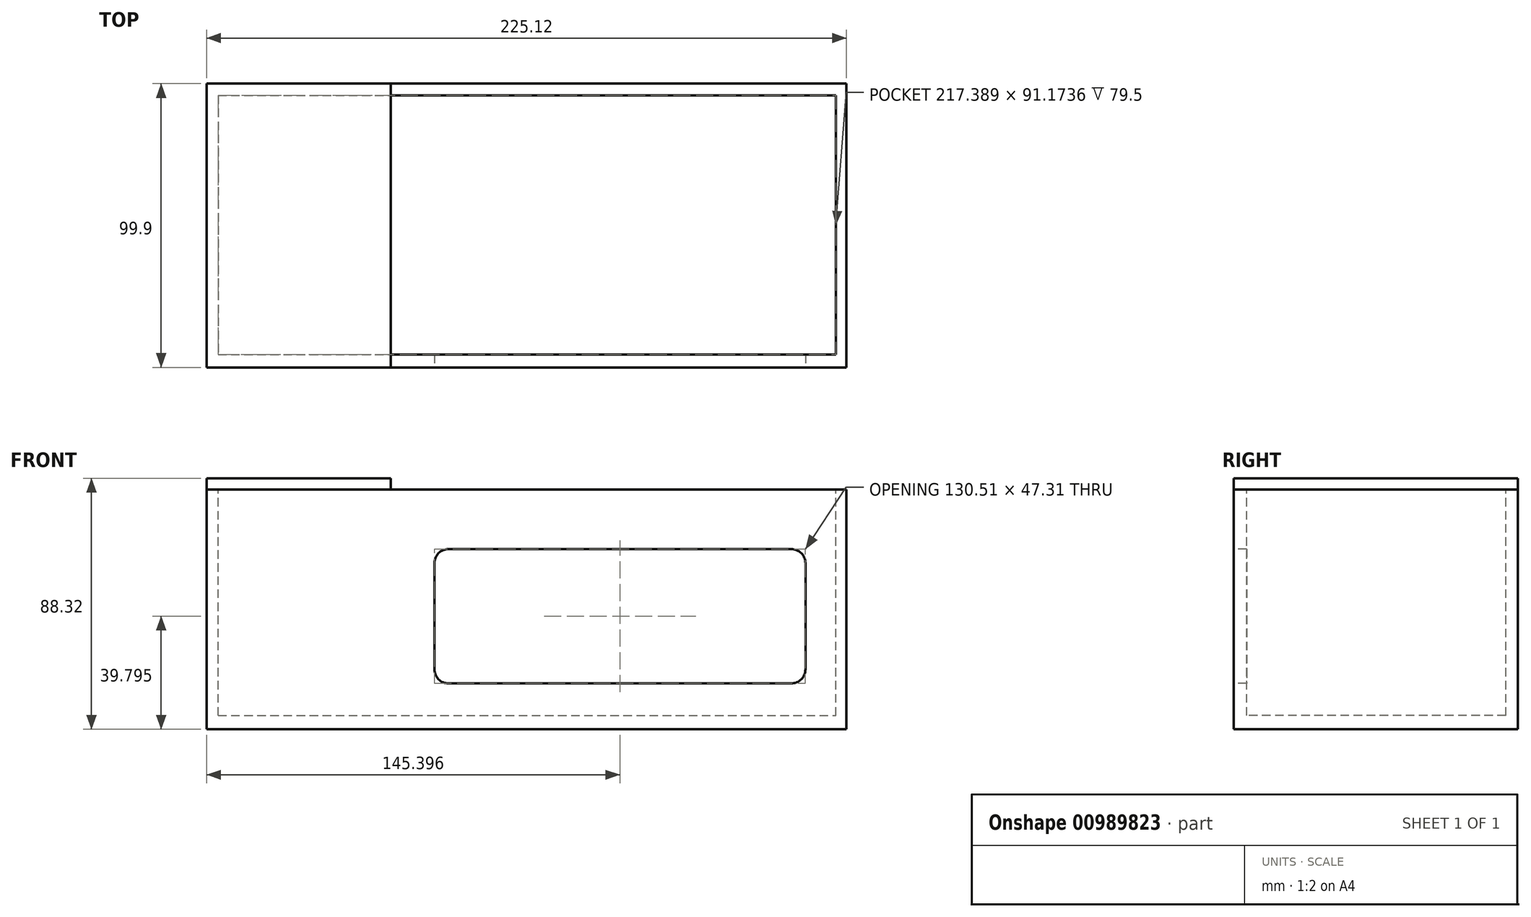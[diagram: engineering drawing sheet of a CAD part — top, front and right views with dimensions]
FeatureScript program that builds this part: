
annotation { "Feature Type Name" : "Feature", "Feature Type Description" : "" }
export const myFeature = defineFeature(function(context is Context, id is Id, definition is map)
    precondition{}
    {
        {
            var Q0;
            Q0=qCreatedBy(makeId("Front.planeOp"),FACE);
            var sketch = newSketch(context, id + "F0", { "sketchPlane" : qUnion([Q0])});
            skLineSegment(sketch, "E0.bottom", {"start": v(112.56, -42.16) * mm, "end": v(-112.56, -42.16) * mm});
            skLineSegment(sketch, "E0.top", {"start": v(112.56, 42.16) * mm, "end": v(-112.56, 42.16) * mm});
            skLineSegment(sketch, "E0.left", {"start": v(112.56, -42.16) * mm, "end": v(112.56, 42.16) * mm});
            skLineSegment(sketch, "E0.right", {"start": v(-112.56, -42.16) * mm, "end": v(-112.56, 42.16) * mm});
            skPoint(sketch, "E0.middle", {"position": v(0, 0) * mm});
            skSolve(sketch);
        }
        {
            var Q0;
            Q0 = qSketchRegion(id + "F0", true);
            extrude(context, id + "F1", {"entities" : qUnion([Q0]), "depth" : 99.9 * mm, "offsetDistance" : 25 * mm});
        }
        {
            var Q0;
            Q0=makeQuery(id+"F1.opExtrude","SWEPT_FACE",FACE,{"disambiguationData":[OSD([sQuery(id+"F0.wireOp",EDGE,"E0.top")])]});
            var sketch = newSketch(context, id + "F2", { "sketchPlane" : qUnion([Q0])});
            skLineSegment(sketch, "E1.bottom", {"start": v(-108.53, -4.18) * mm, "end": v(108.86, -4.18) * mm});
            skLineSegment(sketch, "E1.top", {"start": v(-108.53, -95.35) * mm, "end": v(108.86, -95.35) * mm});
            skLineSegment(sketch, "E1.left", {"start": v(-108.53, -4.18) * mm, "end": v(-108.53, -95.35) * mm});
            skLineSegment(sketch, "E1.right", {"start": v(108.86, -4.18) * mm, "end": v(108.86, -95.35) * mm});
            skSolve(sketch);
        }
        {
            var Q0;
            Q0=makeQuery(id+"F2.imprint","IMPRINT",FACE,{"disambiguationData":[TD([[makeQuery(id+"F2.imprint","IMPRINT",EDGE,{"derivedFrom":sQuery(id+"F2.wireOp",EDGE,"E1.bottom")}),-1.0]])]});
            extrude(context, id + "F3", {"entities" : qUnion([Q0]), "operationType" : NewBodyOperationType.REMOVE, "oppositeDirection" : true, "depth" : 79.5 * mm, "offsetDistance" : 25 * mm});
        }
        {
            var Q0;
            Q0=makeQuery(id+"F1.opExtrude","SWEPT_FACE",FACE,{"disambiguationData":[OSD([sQuery(id+"F0.wireOp",EDGE,"E0.top")])]});
            var sketch = newSketch(context, id + "F4", { "sketchPlane" : qUnion([Q0])});
            skLineSegment(sketch, "E2.bottom", {"start": v(-112.56, 0) * mm, "end": v(-47.75, 0) * mm});
            skLineSegment(sketch, "E2.top", {"start": v(-112.56, -99.9) * mm, "end": v(-47.75, -99.9) * mm});
            skLineSegment(sketch, "E2.left", {"start": v(-112.56, 0) * mm, "end": v(-112.56, -99.9) * mm});
            skLineSegment(sketch, "E2.right", {"start": v(-47.75, 0) * mm, "end": v(-47.75, -99.9) * mm});
            skSolve(sketch);
        }
        {
            var Q0;
            Q0 = qSketchRegion(id + "F4", true);
            extrude(context, id + "F5", {"entities" : qUnion([Q0]), "depth" : 4 * mm, "offsetDistance" : 25 * mm});
        }
        {
            var Q0;
            Q0=makeQuery(id+"F1.opExtrude","CAP_FACE",FACE,{"disambiguationData":[OSD([sQuery(id+"F0.wireOp",EDGE,"E0.bottom"),sQuery(id+"F0.wireOp",EDGE,"E0.top"),sQuery(id+"F0.wireOp",EDGE,"E0.left"),sQuery(id+"F0.wireOp",EDGE,"E0.right")])],"isStart":false});
            var sketch = newSketch(context, id + "F6", { "sketchPlane" : qUnion([Q0])});
            skLineSegment(sketch, "E3.bottom", {"start": v(-32.42, 21.29) * mm, "end": v(98.09, 21.29) * mm});
            skLineSegment(sketch, "E3.top", {"start": v(-32.42, -26.02) * mm, "end": v(98.09, -26.02) * mm});
            skLineSegment(sketch, "E3.left", {"start": v(-32.42, 21.29) * mm, "end": v(-32.42, -26.02) * mm});
            skLineSegment(sketch, "E3.right", {"start": v(98.09, 21.29) * mm, "end": v(98.09, -26.02) * mm});
            skSolve(sketch);
        }
        {
            var Q0;
            Q0 = qSketchRegion(id + "F6", true);
            extrude(context, id + "F7", {"entities" : qUnion([Q0]), "operationType" : NewBodyOperationType.REMOVE, "oppositeDirection" : true, "depth" : 25 * mm, "offsetDistance" : 25 * mm});
        }
        {
            var Q0;
            Q0=makeQuery(id+"F7.boolean.opBoolean","COPY",EDGE,{"derivedFrom":makeQuery(id+"F7.opExtrude","SWEPT_EDGE",EDGE,{"disambiguationData":[OSD([sQuery(id+"F6.wireOp",EDGE,"E3.top"),sQuery(id+"F6.wireOp",EDGE,"E3.left")])]})});
            var Q1;
            Q1=makeQuery(id+"F7.boolean.opBoolean","COPY",EDGE,{"derivedFrom":makeQuery(id+"F7.opExtrude","SWEPT_EDGE",EDGE,{"disambiguationData":[OSD([sQuery(id+"F6.wireOp",EDGE,"E3.bottom"),sQuery(id+"F6.wireOp",EDGE,"E3.left")])]})});
            var Q2;
            Q2=makeQuery(id+"F7.boolean.opBoolean","COPY",EDGE,{"derivedFrom":makeQuery(id+"F7.opExtrude","SWEPT_EDGE",EDGE,{"disambiguationData":[OSD([sQuery(id+"F6.wireOp",EDGE,"E3.bottom"),sQuery(id+"F6.wireOp",EDGE,"E3.right")])]})});
            var Q3;
            Q3=makeQuery(id+"F7.boolean.opBoolean","COPY",EDGE,{"derivedFrom":makeQuery(id+"F7.opExtrude","SWEPT_EDGE",EDGE,{"disambiguationData":[OSD([sQuery(id+"F6.wireOp",EDGE,"E3.top"),sQuery(id+"F6.wireOp",EDGE,"E3.right")])]})});
            fillet(context, id + "F8", {"entities" : qUnion([Q0, Q1, Q2, Q3]), "radius" : 5 * mm, "tangentPropagation" : true, "allowEdgeOverflow" : false});
        }
    });
